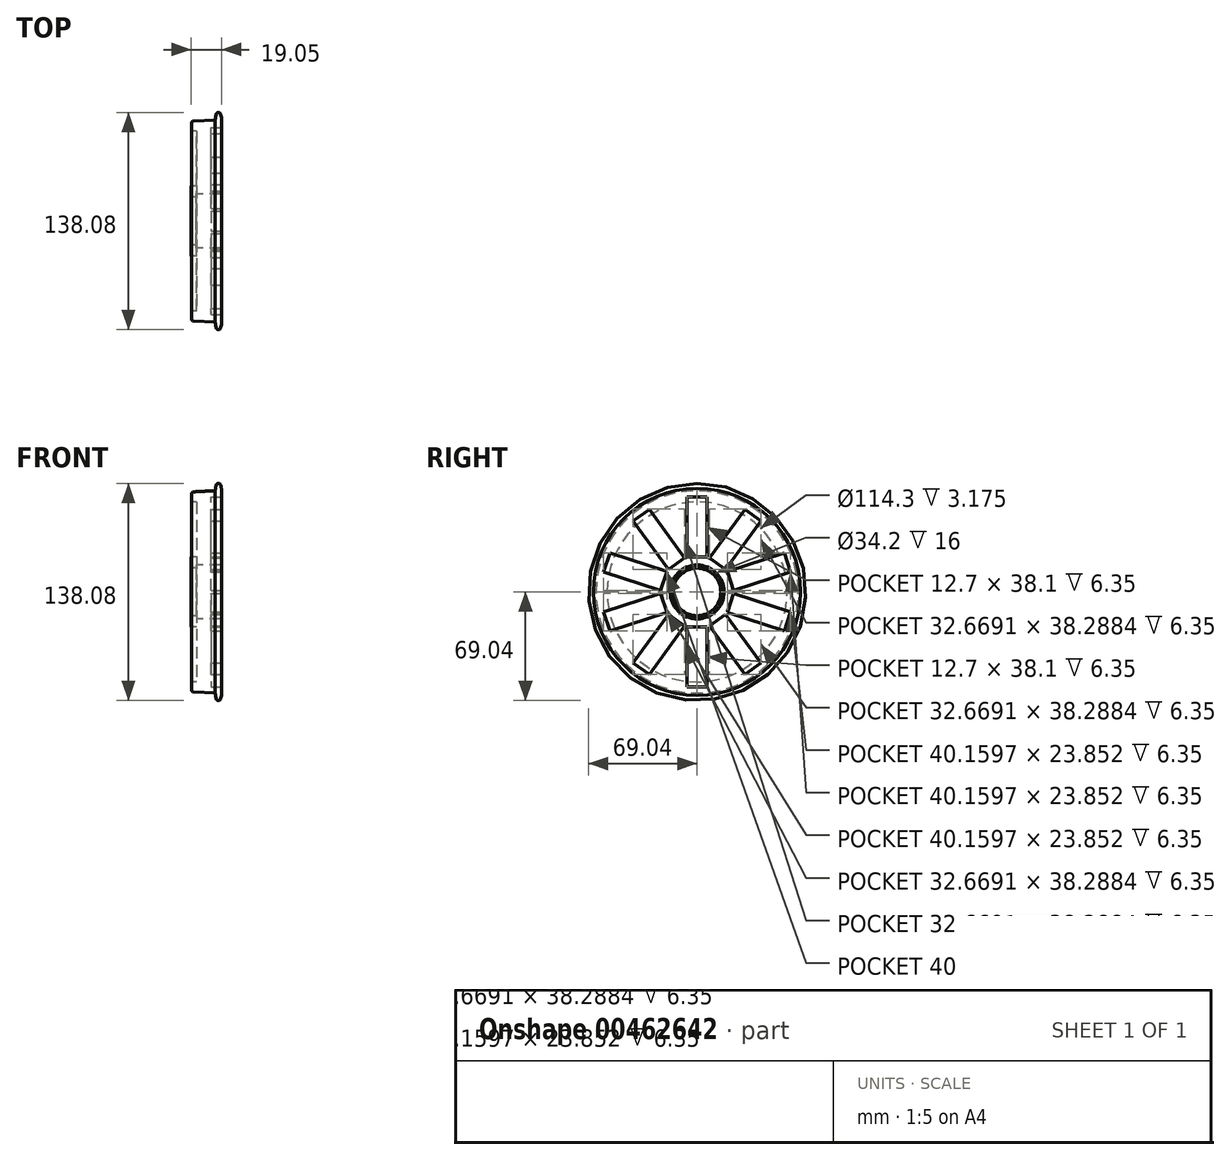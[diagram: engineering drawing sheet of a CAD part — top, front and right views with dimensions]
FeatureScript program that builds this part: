
annotation { "Feature Type Name" : "Feature", "Feature Type Description" : "" }
export const myFeature = defineFeature(function(context is Context, id is Id, definition is map)
    precondition{}
    {
        {
            var Q0;
            Q0=qCreatedBy(makeId("Front.planeOp"),FACE);
            var sketch = newSketch(context, id + "F0", { "sketchPlane" : qUnion([Q0])});
            skLineSegment(sketch, "E0", {"start": v(-70.3, 0) * mm, "end": v(73.77, 0) * mm, "construction": true});
            skLineSegment(sketch, "E1", {"start": v(18.95, 17.1) * mm, "end": v(18.95, 65.79) * mm});
            skLineSegment(sketch, "E2", {"start": v(18.95, 65.79) * mm, "end": v(18.6, 67.78) * mm});
            skArc(sketch, "E3", {"start": v(18.6, 67.78) * mm, "mid": v(17.1, 69.04) * mm, "end": v(15.6, 67.78) * mm});
            skLineSegment(sketch, "E4", {"start": v(15.6, 67.78) * mm, "end": v(14.99, 64.29) * mm});
            skLineSegment(sketch, "E5", {"start": v(14.99, 64.29) * mm, "end": v(1.2, 63.56) * mm});
            skLineSegment(sketch, "E6", {"start": v(17.1, 69.04) * mm, "end": v(-20.65, 69.04) * mm, "construction": true});
            skLineSegment(sketch, "E7", {"start": v(0, 62.3) * mm, "end": v(0, 57.15) * mm});
            skLineSegment(sketch, "E8", {"start": v(0, 57.15) * mm, "end": v(3.18, 57.15) * mm});
            skLineSegment(sketch, "E9", {"start": v(3.18, 57.15) * mm, "end": v(3.18, 22.18) * mm});
            skPoint(sketch, "E10.visualSharp", {"position": v(0, 63.5) * mm});
            skArc(sketch, "E10.filletArc", {"start": v(1.2, 63.56) * mm, "mid": v(0.35, 63.17) * mm, "end": v(0, 62.3) * mm});
            skLineSegment(sketch, "E11", {"start": v(18.95, 17.1) * mm, "end": v(2.95, 17.1) * mm});
            skLineSegment(sketch, "E12", {"start": v(-0.1, 17.1) * mm, "end": v(-0.1, 22.18) * mm});
            skLineSegment(sketch, "E13", {"start": v(-0.1, 22.18) * mm, "end": v(3.18, 22.18) * mm});
            skLineSegment(sketch, "E14.bottom", {"start": v(-0.1, 17.1) * mm, "end": v(-0.1, 17.1) * mm});
            skLineSegment(sketch, "E14.top", {"start": v(-0.1, 15.1) * mm, "end": v(2.95, 15.1) * mm});
            skLineSegment(sketch, "E14.left", {"start": v(-0.1, 17.1) * mm, "end": v(-0.1, 15.1) * mm});
            skLineSegment(sketch, "E14.right", {"start": v(2.95, 17.1) * mm, "end": v(2.95, 15.1) * mm});
            skLineSegment(sketch, "E15", {"start": v(2.95, 17.1) * mm, "end": v(2.95, 17.1) * mm});
            skSolve(sketch);
        }
        {
            var Q0;
            Q0=makeQuery(id+"F0.imprint","IMPRINT",FACE,{"disambiguationData":[TD([[makeQuery(id+"F0.imprint","IMPRINT",EDGE,{"derivedFrom":sQuery(id+"F0.wireOp",EDGE,"E1")}),1.0]])]});
            var Q1;
            Q1=sQuery(id+"F0.wireOp",EDGE,"E0");
            revolve(context, id + "F1", {"entities" : qUnion([Q0]), "axis" : qUnion([Q1]), "revolveType" : RevolveType.FULL});
        }
        {
            var Q0;
            Q0=makeQuery(id+"F1.opRevolve","SWEPT_FACE",FACE,{"disambiguationData":[OSD([sQuery(id+"F0.wireOp",EDGE,"E1")])]});
            var sketch = newSketch(context, id + "F2", { "sketchPlane" : qUnion([Q0])});
            skCircle(sketch, "E16", {"center": v(0, 0) * mm, "radius": 41.28 * mm, "construction": true});
            skLineSegment(sketch, "E17.bottom", {"start": v(6.35, 22.23) * mm, "end": v(-6.35, 22.23) * mm});
            skLineSegment(sketch, "E17.top", {"start": v(6.35, 60.33) * mm, "end": v(-6.35, 60.33) * mm});
            skLineSegment(sketch, "E17.left", {"start": v(6.35, 22.23) * mm, "end": v(6.35, 60.33) * mm});
            skLineSegment(sketch, "E17.right", {"start": v(-6.35, 22.23) * mm, "end": v(-6.35, 60.33) * mm});
            skPoint(sketch, "E17.middle", {"position": v(0, 41.28) * mm});
            skLineSegment(sketch, "E18.1.0", {"start": v(-18.2, 14.25) * mm, "end": v(-40.6, 45.07) * mm});
            skLineSegment(sketch, "E18.1.1", {"start": v(-7.93, 21.71) * mm, "end": v(-30.32, 52.54) * mm});
            skLineSegment(sketch, "E18.1.2", {"start": v(-30.32, 52.54) * mm, "end": v(-40.6, 45.07) * mm});
            skLineSegment(sketch, "E18.1.3", {"start": v(-7.93, 21.71) * mm, "end": v(-18.2, 14.25) * mm});
            skPoint(sketch, "E18.1.4", {"position": v(-24.26, 33.4) * mm});
            skLineSegment(sketch, "E18.2.0", {"start": v(-23.1, 0.83) * mm, "end": v(-59.33, 12.6) * mm});
            skLineSegment(sketch, "E18.2.1", {"start": v(-19.17, 12.9) * mm, "end": v(-55.41, 24.68) * mm});
            skLineSegment(sketch, "E18.2.2", {"start": v(-55.41, 24.68) * mm, "end": v(-59.33, 12.6) * mm});
            skLineSegment(sketch, "E18.2.3", {"start": v(-19.17, 12.9) * mm, "end": v(-23.1, 0.83) * mm});
            skPoint(sketch, "E18.2.4", {"position": v(-39.25, 12.75) * mm});
            skLineSegment(sketch, "E18.3.0", {"start": v(-19.17, -12.9) * mm, "end": v(-55.41, -24.68) * mm});
            skLineSegment(sketch, "E18.3.1", {"start": v(-23.1, -0.83) * mm, "end": v(-59.33, -12.6) * mm});
            skLineSegment(sketch, "E18.3.2", {"start": v(-59.33, -12.6) * mm, "end": v(-55.41, -24.68) * mm});
            skLineSegment(sketch, "E18.3.3", {"start": v(-23.1, -0.83) * mm, "end": v(-19.17, -12.9) * mm});
            skPoint(sketch, "E18.3.4", {"position": v(-39.25, -12.75) * mm});
            skLineSegment(sketch, "E18.4.0", {"start": v(-7.93, -21.71) * mm, "end": v(-30.32, -52.54) * mm});
            skLineSegment(sketch, "E18.4.1", {"start": v(-18.2, -14.25) * mm, "end": v(-40.6, -45.07) * mm});
            skLineSegment(sketch, "E18.4.2", {"start": v(-40.6, -45.07) * mm, "end": v(-30.32, -52.54) * mm});
            skLineSegment(sketch, "E18.4.3", {"start": v(-18.2, -14.25) * mm, "end": v(-7.93, -21.71) * mm});
            skPoint(sketch, "E18.4.4", {"position": v(-24.26, -33.4) * mm});
            skLineSegment(sketch, "E18.5.0", {"start": v(6.35, -22.23) * mm, "end": v(6.35, -60.33) * mm});
            skLineSegment(sketch, "E18.5.1", {"start": v(-6.35, -22.23) * mm, "end": v(-6.35, -60.33) * mm});
            skLineSegment(sketch, "E18.5.2", {"start": v(-6.35, -60.33) * mm, "end": v(6.35, -60.33) * mm});
            skLineSegment(sketch, "E18.5.3", {"start": v(-6.35, -22.23) * mm, "end": v(6.35, -22.23) * mm});
            skPoint(sketch, "E18.5.4", {"position": v(0, -41.28) * mm});
            skLineSegment(sketch, "E18.6.0", {"start": v(18.2, -14.25) * mm, "end": v(40.6, -45.07) * mm});
            skLineSegment(sketch, "E18.6.1", {"start": v(7.93, -21.71) * mm, "end": v(30.32, -52.54) * mm});
            skLineSegment(sketch, "E18.6.2", {"start": v(30.32, -52.54) * mm, "end": v(40.6, -45.07) * mm});
            skLineSegment(sketch, "E18.6.3", {"start": v(7.93, -21.71) * mm, "end": v(18.2, -14.25) * mm});
            skPoint(sketch, "E18.6.4", {"position": v(24.26, -33.4) * mm});
            skLineSegment(sketch, "E18.7.0", {"start": v(23.1, -0.83) * mm, "end": v(59.33, -12.6) * mm});
            skLineSegment(sketch, "E18.7.1", {"start": v(19.17, -12.9) * mm, "end": v(55.41, -24.68) * mm});
            skLineSegment(sketch, "E18.7.2", {"start": v(55.41, -24.68) * mm, "end": v(59.33, -12.6) * mm});
            skLineSegment(sketch, "E18.7.3", {"start": v(19.17, -12.9) * mm, "end": v(23.1, -0.83) * mm});
            skPoint(sketch, "E18.7.4", {"position": v(39.25, -12.75) * mm});
            skLineSegment(sketch, "E18.8.0", {"start": v(19.17, 12.9) * mm, "end": v(55.41, 24.68) * mm});
            skLineSegment(sketch, "E18.8.1", {"start": v(23.1, 0.83) * mm, "end": v(59.33, 12.6) * mm});
            skLineSegment(sketch, "E18.8.2", {"start": v(59.33, 12.6) * mm, "end": v(55.41, 24.68) * mm});
            skLineSegment(sketch, "E18.8.3", {"start": v(23.1, 0.83) * mm, "end": v(19.17, 12.9) * mm});
            skPoint(sketch, "E18.8.4", {"position": v(39.25, 12.75) * mm});
            skLineSegment(sketch, "E18.9.0", {"start": v(7.93, 21.71) * mm, "end": v(30.32, 52.54) * mm});
            skLineSegment(sketch, "E18.9.1", {"start": v(18.2, 14.25) * mm, "end": v(40.6, 45.07) * mm});
            skLineSegment(sketch, "E18.9.2", {"start": v(40.6, 45.07) * mm, "end": v(30.32, 52.54) * mm});
            skLineSegment(sketch, "E18.9.3", {"start": v(18.2, 14.25) * mm, "end": v(7.93, 21.71) * mm});
            skPoint(sketch, "E18.9.4", {"position": v(24.26, 33.4) * mm});
            skSolve(sketch);
        }
        {
            var Q0;
            Q0 = qSketchRegion(id + "F2", true);
            extrude(context, id + "F3", {"entities" : qUnion([Q0]), "operationType" : NewBodyOperationType.REMOVE, "oppositeDirection" : true, "depth" : 6.35 * mm});
        }
    });
